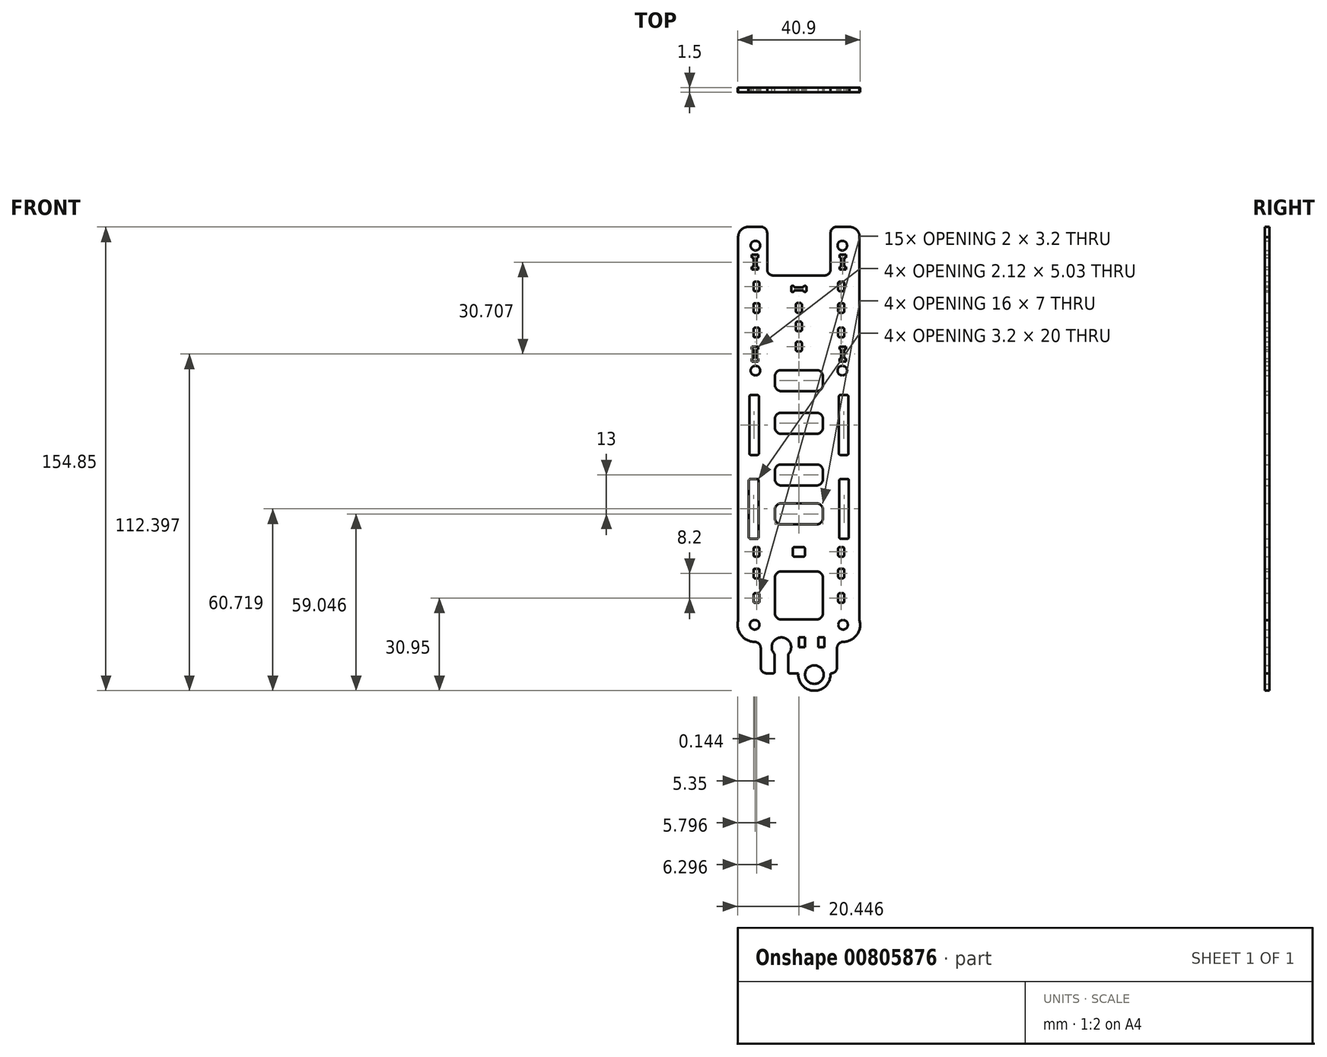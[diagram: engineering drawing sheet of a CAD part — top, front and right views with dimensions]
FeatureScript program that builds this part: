
annotation { "Feature Type Name" : "Feature", "Feature Type Description" : "" }
export const myFeature = defineFeature(function(context is Context, id is Id, definition is map)
    precondition{}
    {
        {
            var Q0;
            Q0=qCreatedBy(makeId("Front.planeOp"),FACE);
            var sketch = newSketch(context, id + "F0", { "sketchPlane" : qUnion([Q0])});
            skLineSegment(sketch, "E0", {"start": v(-16.2, 27.54) * mm, "end": v(-14.07, 27.54) * mm});
            skLineSegment(sketch, "E1", {"start": v(-14.07, 27.54) * mm, "end": v(-14.07, 26.54) * mm});
            skLineSegment(sketch, "E2", {"start": v(-14.07, 26.54) * mm, "end": v(-14.63, 26.54) * mm});
            skLineSegment(sketch, "E3", {"start": v(-14.63, 26.54) * mm, "end": v(-14.63, 23.51) * mm});
            skLineSegment(sketch, "E4", {"start": v(-14.63, 23.51) * mm, "end": v(-14.07, 23.51) * mm});
            skLineSegment(sketch, "E5", {"start": v(-14.07, 23.51) * mm, "end": v(-14.07, 22.51) * mm});
            skLineSegment(sketch, "E6", {"start": v(-14.07, 22.51) * mm, "end": v(-16.2, 22.51) * mm});
            skLineSegment(sketch, "E7", {"start": v(-16.2, 22.51) * mm, "end": v(-16.2, 23.51) * mm});
            skLineSegment(sketch, "E8", {"start": v(-16.2, 23.51) * mm, "end": v(-15.63, 23.51) * mm});
            skLineSegment(sketch, "E9", {"start": v(-15.63, 23.51) * mm, "end": v(-15.63, 26.54) * mm});
            skLineSegment(sketch, "E10", {"start": v(-15.63, 26.54) * mm, "end": v(-16.2, 26.54) * mm});
            skLineSegment(sketch, "E11", {"start": v(-16.2, 26.54) * mm, "end": v(-16.2, 27.54) * mm});
            skLineSegment(sketch, "E12", {"start": v(-20.32, 40.38) * mm, "end": v(19.03, 40.38) * mm, "construction": true});
            skLineSegment(sketch, "E13.MirrorCS", {"start": v(13.67, 23.51) * mm, "end": v(13.1, 23.51) * mm});
            skLineSegment(sketch, "E14.MirrorCS", {"start": v(15.23, 23.51) * mm, "end": v(14.67, 23.51) * mm});
            skLineSegment(sketch, "E15.MirrorCS", {"start": v(13.1, 23.51) * mm, "end": v(13.1, 22.51) * mm});
            skLineSegment(sketch, "E16.MirrorCS", {"start": v(15.23, 27.54) * mm, "end": v(13.1, 27.54) * mm});
            skLineSegment(sketch, "E17.MirrorCS", {"start": v(14.67, 26.54) * mm, "end": v(15.23, 26.54) * mm});
            skLineSegment(sketch, "E18.MirrorCS", {"start": v(15.23, 26.54) * mm, "end": v(15.23, 27.54) * mm});
            skLineSegment(sketch, "E19.MirrorCS", {"start": v(13.1, 22.51) * mm, "end": v(15.23, 22.51) * mm});
            skLineSegment(sketch, "E20.MirrorCS", {"start": v(15.23, 22.51) * mm, "end": v(15.23, 23.51) * mm});
            skLineSegment(sketch, "E21.MirrorCS", {"start": v(13.1, 27.54) * mm, "end": v(13.1, 26.54) * mm});
            skLineSegment(sketch, "E22.MirrorCS", {"start": v(13.1, 26.54) * mm, "end": v(13.67, 26.54) * mm});
            skLineSegment(sketch, "E23.MirrorCS", {"start": v(13.67, 26.54) * mm, "end": v(13.67, 23.51) * mm});
            skLineSegment(sketch, "E24.MirrorCS", {"start": v(14.67, 23.51) * mm, "end": v(14.67, 26.54) * mm});
            skLineSegment(sketch, "E25.MirrorCS", {"start": v(-14.63, 57.25) * mm, "end": v(-14.07, 57.25) * mm});
            skLineSegment(sketch, "E26.MirrorCS", {"start": v(-14.63, 54.22) * mm, "end": v(-14.63, 57.25) * mm});
            skLineSegment(sketch, "E27.MirrorCS", {"start": v(-14.07, 54.22) * mm, "end": v(-14.63, 54.22) * mm});
            skLineSegment(sketch, "E28.MirrorCS", {"start": v(-14.07, 53.22) * mm, "end": v(-14.07, 54.22) * mm});
            skLineSegment(sketch, "E29.MirrorCS", {"start": v(-16.2, 53.22) * mm, "end": v(-14.07, 53.22) * mm});
            skLineSegment(sketch, "E30.MirrorCS", {"start": v(-16.2, 54.22) * mm, "end": v(-16.2, 53.22) * mm});
            skLineSegment(sketch, "E31.MirrorCS", {"start": v(-14.07, 57.25) * mm, "end": v(-14.07, 58.25) * mm});
            skLineSegment(sketch, "E32.MirrorCS", {"start": v(-14.07, 58.25) * mm, "end": v(-16.2, 58.25) * mm});
            skLineSegment(sketch, "E33.MirrorCS", {"start": v(-15.63, 54.22) * mm, "end": v(-16.2, 54.22) * mm});
            skLineSegment(sketch, "E34.MirrorCS", {"start": v(-16.2, 58.25) * mm, "end": v(-16.2, 57.25) * mm});
            skLineSegment(sketch, "E35.MirrorCS", {"start": v(-16.2, 57.25) * mm, "end": v(-15.63, 57.25) * mm});
            skLineSegment(sketch, "E36.MirrorCS", {"start": v(-15.63, 57.25) * mm, "end": v(-15.63, 54.22) * mm});
            skLineSegment(sketch, "E37.MirrorCS", {"start": v(14.67, 54.22) * mm, "end": v(15.23, 54.22) * mm});
            skLineSegment(sketch, "E38.MirrorCS", {"start": v(14.67, 57.25) * mm, "end": v(14.67, 54.22) * mm});
            skLineSegment(sketch, "E39.MirrorCS", {"start": v(15.23, 53.22) * mm, "end": v(13.1, 53.22) * mm});
            skLineSegment(sketch, "E40.MirrorCS", {"start": v(15.23, 58.25) * mm, "end": v(15.23, 57.25) * mm});
            skLineSegment(sketch, "E41.MirrorCS", {"start": v(13.67, 54.22) * mm, "end": v(13.67, 57.25) * mm});
            skLineSegment(sketch, "E42.MirrorCS", {"start": v(13.1, 58.25) * mm, "end": v(15.23, 58.25) * mm});
            skLineSegment(sketch, "E43.MirrorCS", {"start": v(13.1, 57.25) * mm, "end": v(13.1, 58.25) * mm});
            skLineSegment(sketch, "E44.MirrorCS", {"start": v(13.1, 53.22) * mm, "end": v(13.1, 54.22) * mm});
            skLineSegment(sketch, "E45.MirrorCS", {"start": v(13.67, 57.25) * mm, "end": v(13.1, 57.25) * mm});
            skLineSegment(sketch, "E46.MirrorCS", {"start": v(15.23, 57.25) * mm, "end": v(14.67, 57.25) * mm});
            skLineSegment(sketch, "E47.MirrorCS", {"start": v(13.1, 54.22) * mm, "end": v(13.67, 54.22) * mm});
            skLineSegment(sketch, "E48.MirrorCS", {"start": v(15.23, 54.22) * mm, "end": v(15.23, 53.22) * mm});
            skCircle(sketch, "E49", {"center": v(-14.98, 61.25) * mm, "radius": 1.6 * mm});
            skCircle(sketch, "E50.MirrorC", {"center": v(14.02, 61.25) * mm, "radius": 1.6 * mm});
            skCircle(sketch, "E51", {"center": v(-15.23, -65.35) * mm, "radius": 1.6 * mm});
            skCircle(sketch, "E52.MirrorC", {"center": v(14.27, -65.35) * mm, "radius": 1.6 * mm});
            skLineSegment(sketch, "E53.bottom", {"start": v(-15.13, -39.42) * mm, "end": v(-14.13, -39.42) * mm});
            skLineSegment(sketch, "E53.top", {"start": v(-15.13, -42.62) * mm, "end": v(-14.13, -42.62) * mm});
            skLineSegment(sketch, "E53.left", {"start": v(-15.63, -39.92) * mm, "end": v(-15.63, -42.12) * mm});
            skLineSegment(sketch, "E53.right", {"start": v(-13.63, -39.92) * mm, "end": v(-13.63, -42.12) * mm});
            skLineSegment(sketch, "E54.bottom", {"start": v(-15.13, -46.62) * mm, "end": v(-14.13, -46.62) * mm});
            skLineSegment(sketch, "E54.top", {"start": v(-15.13, -49.82) * mm, "end": v(-14.13, -49.82) * mm});
            skLineSegment(sketch, "E54.left", {"start": v(-15.63, -47.12) * mm, "end": v(-15.63, -49.32) * mm});
            skLineSegment(sketch, "E54.right", {"start": v(-13.63, -47.12) * mm, "end": v(-13.63, -49.32) * mm});
            skLineSegment(sketch, "E55.bottom", {"start": v(-15.13, -54.82) * mm, "end": v(-14.13, -54.82) * mm});
            skLineSegment(sketch, "E55.top", {"start": v(-15.13, -58.02) * mm, "end": v(-14.13, -58.02) * mm});
            skLineSegment(sketch, "E55.left", {"start": v(-15.63, -55.32) * mm, "end": v(-15.63, -57.52) * mm});
            skLineSegment(sketch, "E55.right", {"start": v(-13.63, -55.32) * mm, "end": v(-13.63, -57.52) * mm});
            skPoint(sketch, "E56.visualSharp", {"position": v(-15.63, -39.42) * mm});
            skArc(sketch, "E56.filletArc", {"start": v(-15.13, -39.42) * mm, "mid": v(-15.49, -39.57) * mm, "end": v(-15.63, -39.92) * mm});
            skPoint(sketch, "E57.visualSharp", {"position": v(-13.63, -39.42) * mm});
            skArc(sketch, "E57.filletArc", {"start": v(-13.63, -39.92) * mm, "mid": v(-13.78, -39.57) * mm, "end": v(-14.13, -39.42) * mm});
            skPoint(sketch, "E58.visualSharp", {"position": v(-13.63, -42.62) * mm});
            skArc(sketch, "E58.filletArc", {"start": v(-14.13, -42.62) * mm, "mid": v(-13.78, -42.47) * mm, "end": v(-13.63, -42.12) * mm});
            skPoint(sketch, "E59.visualSharp", {"position": v(-15.63, -42.62) * mm});
            skArc(sketch, "E59.filletArc", {"start": v(-15.63, -42.12) * mm, "mid": v(-15.49, -42.47) * mm, "end": v(-15.13, -42.62) * mm});
            skPoint(sketch, "E60.visualSharp", {"position": v(-15.63, -46.62) * mm});
            skArc(sketch, "E60.filletArc", {"start": v(-15.13, -46.62) * mm, "mid": v(-15.49, -46.77) * mm, "end": v(-15.63, -47.12) * mm});
            skPoint(sketch, "E61.visualSharp", {"position": v(-13.63, -46.62) * mm});
            skArc(sketch, "E61.filletArc", {"start": v(-13.63, -47.12) * mm, "mid": v(-13.78, -46.77) * mm, "end": v(-14.13, -46.62) * mm});
            skPoint(sketch, "E62.visualSharp", {"position": v(-13.63, -49.82) * mm});
            skArc(sketch, "E62.filletArc", {"start": v(-14.13, -49.82) * mm, "mid": v(-13.78, -49.67) * mm, "end": v(-13.63, -49.32) * mm});
            skPoint(sketch, "E63.visualSharp", {"position": v(-15.63, -49.82) * mm});
            skArc(sketch, "E63.filletArc", {"start": v(-15.63, -49.32) * mm, "mid": v(-15.49, -49.67) * mm, "end": v(-15.13, -49.82) * mm});
            skPoint(sketch, "E64.visualSharp", {"position": v(-15.63, -54.82) * mm});
            skArc(sketch, "E64.filletArc", {"start": v(-15.13, -54.82) * mm, "mid": v(-15.49, -54.97) * mm, "end": v(-15.63, -55.32) * mm});
            skPoint(sketch, "E65.visualSharp", {"position": v(-13.63, -54.82) * mm});
            skArc(sketch, "E65.filletArc", {"start": v(-13.63, -55.32) * mm, "mid": v(-13.78, -54.97) * mm, "end": v(-14.13, -54.82) * mm});
            skPoint(sketch, "E66.visualSharp", {"position": v(-13.63, -58.02) * mm});
            skArc(sketch, "E66.filletArc", {"start": v(-14.13, -58.02) * mm, "mid": v(-13.78, -57.87) * mm, "end": v(-13.63, -57.52) * mm});
            skPoint(sketch, "E67.visualSharp", {"position": v(-15.63, -58.02) * mm});
            skArc(sketch, "E67.filletArc", {"start": v(-15.63, -57.52) * mm, "mid": v(-15.49, -57.87) * mm, "end": v(-15.13, -58.02) * mm});
            skArc(sketch, "E68.MirrorCS", {"start": v(14.17, -54.82) * mm, "mid": v(14.52, -54.97) * mm, "end": v(14.67, -55.32) * mm});
            skArc(sketch, "E69.MirrorCS", {"start": v(13.17, -58.02) * mm, "mid": v(12.81, -57.87) * mm, "end": v(12.67, -57.52) * mm});
            skArc(sketch, "E70.MirrorCS", {"start": v(12.67, -39.92) * mm, "mid": v(12.81, -39.57) * mm, "end": v(13.17, -39.42) * mm});
            skArc(sketch, "E71.MirrorCS", {"start": v(14.17, -39.42) * mm, "mid": v(14.52, -39.57) * mm, "end": v(14.67, -39.92) * mm});
            skArc(sketch, "E72.MirrorCS", {"start": v(14.67, -49.32) * mm, "mid": v(14.52, -49.67) * mm, "end": v(14.17, -49.82) * mm});
            skArc(sketch, "E73.MirrorCS", {"start": v(12.67, -55.32) * mm, "mid": v(12.81, -54.97) * mm, "end": v(13.17, -54.82) * mm});
            skArc(sketch, "E74.MirrorCS", {"start": v(14.67, -57.52) * mm, "mid": v(14.52, -57.87) * mm, "end": v(14.17, -58.02) * mm});
            skArc(sketch, "E75.MirrorCS", {"start": v(13.17, -42.62) * mm, "mid": v(12.81, -42.47) * mm, "end": v(12.67, -42.12) * mm});
            skArc(sketch, "E76.MirrorCS", {"start": v(13.17, -49.82) * mm, "mid": v(12.81, -49.67) * mm, "end": v(12.67, -49.32) * mm});
            skArc(sketch, "E77.MirrorCS", {"start": v(12.67, -47.12) * mm, "mid": v(12.81, -46.77) * mm, "end": v(13.17, -46.62) * mm});
            skArc(sketch, "E78.MirrorCS", {"start": v(14.17, -46.62) * mm, "mid": v(14.52, -46.77) * mm, "end": v(14.67, -47.12) * mm});
            skArc(sketch, "E79.MirrorCS", {"start": v(14.67, -42.12) * mm, "mid": v(14.52, -42.47) * mm, "end": v(14.17, -42.62) * mm});
            skPoint(sketch, "E80.MirrorP", {"position": v(12.67, -46.62) * mm});
            skLineSegment(sketch, "E81.MirrorCS", {"start": v(14.17, -46.62) * mm, "end": v(13.17, -46.62) * mm});
            skLineSegment(sketch, "E82.MirrorCS", {"start": v(14.67, -47.12) * mm, "end": v(14.67, -49.32) * mm});
            skPoint(sketch, "E83.MirrorP", {"position": v(14.67, -54.82) * mm});
            skPoint(sketch, "E84.MirrorP", {"position": v(14.67, -39.42) * mm});
            skLineSegment(sketch, "E85.MirrorCS", {"start": v(12.67, -39.92) * mm, "end": v(12.67, -42.12) * mm});
            skPoint(sketch, "E86.MirrorP", {"position": v(12.67, -58.02) * mm});
            skLineSegment(sketch, "E87.MirrorCS", {"start": v(14.17, -49.82) * mm, "end": v(13.17, -49.82) * mm});
            skPoint(sketch, "E88.MirrorP", {"position": v(12.67, -42.62) * mm});
            skLineSegment(sketch, "E89.MirrorCS", {"start": v(14.17, -39.42) * mm, "end": v(13.17, -39.42) * mm});
            skPoint(sketch, "E90.MirrorP", {"position": v(14.67, -42.62) * mm});
            skPoint(sketch, "E91.MirrorP", {"position": v(14.67, -58.02) * mm});
            skLineSegment(sketch, "E92.MirrorCS", {"start": v(12.67, -47.12) * mm, "end": v(12.67, -49.32) * mm});
            skPoint(sketch, "E93.MirrorP", {"position": v(12.67, -39.42) * mm});
            skPoint(sketch, "E94.MirrorP", {"position": v(12.67, -54.82) * mm});
            skLineSegment(sketch, "E95.MirrorCS", {"start": v(12.67, -55.32) * mm, "end": v(12.67, -57.52) * mm});
            skPoint(sketch, "E96.MirrorP", {"position": v(14.67, -46.62) * mm});
            skLineSegment(sketch, "E97.MirrorCS", {"start": v(14.67, -39.92) * mm, "end": v(14.67, -42.12) * mm});
            skLineSegment(sketch, "E98.MirrorCS", {"start": v(14.17, -58.02) * mm, "end": v(13.17, -58.02) * mm});
            skLineSegment(sketch, "E99.MirrorCS", {"start": v(14.67, -55.32) * mm, "end": v(14.67, -57.52) * mm});
            skPoint(sketch, "E100.MirrorP", {"position": v(14.67, -49.82) * mm});
            skLineSegment(sketch, "E101.MirrorCS", {"start": v(14.17, -42.62) * mm, "end": v(13.17, -42.62) * mm});
            skPoint(sketch, "E102.MirrorP", {"position": v(12.67, -49.82) * mm});
            skLineSegment(sketch, "E103.MirrorCS", {"start": v(14.17, -54.82) * mm, "end": v(13.17, -54.82) * mm});
            skLineSegment(sketch, "E104", {"start": v(-20.73, 64.37) * mm, "end": v(-20.73, -63.85) * mm});
            skLineSegment(sketch, "E105.MirrorCS", {"start": v(19.77, 64.37) * mm, "end": v(19.77, -63.85) * mm});
            skArc(sketch, "E106", {"start": v(-17.39, 67.48) * mm, "mid": v(-19.81, 66.5) * mm, "end": v(-20.73, 64.04) * mm});
            skArc(sketch, "E107.MirrorCS", {"start": v(16.42, 67.48) * mm, "mid": v(18.84, 66.5) * mm, "end": v(19.77, 64.04) * mm});
            skPoint(sketch, "E108.orphan", {"position": v(-20.73, 67.03) * mm});
            skPoint(sketch, "E109.orphan", {"position": v(19.77, 67.03) * mm});
            skLineSegment(sketch, "E110", {"start": v(-17.39, 67.48) * mm, "end": v(-13.07, 67.48) * mm});
            skLineSegment(sketch, "E111", {"start": v(-11.07, 65.48) * mm, "end": v(-11.07, 53.27) * mm});
            skLineSegment(sketch, "E112", {"start": v(-9.07, 51.27) * mm, "end": v(-0.48, 51.27) * mm});
            skLineSegment(sketch, "E113.MirrorCS", {"start": v(16.42, 67.48) * mm, "end": v(12.1, 67.48) * mm});
            skLineSegment(sketch, "E114.MirrorCS", {"start": v(10.1, 65.48) * mm, "end": v(10.1, 53.27) * mm});
            skLineSegment(sketch, "E115.MirrorCS", {"start": v(8.1, 51.27) * mm, "end": v(-0.48, 51.27) * mm});
            skPoint(sketch, "E116.orphan", {"position": v(-14.5, 62.78) * mm});
            skPoint(sketch, "E117.orphan", {"position": v(13.54, 62.78) * mm});
            skPoint(sketch, "E118.visualSharp", {"position": v(-11.07, 67.48) * mm});
            skArc(sketch, "E118.filletArc", {"start": v(-11.07, 65.48) * mm, "mid": v(-11.65, 66.9) * mm, "end": v(-13.07, 67.48) * mm});
            skPoint(sketch, "E119.visualSharp", {"position": v(10.1, 67.48) * mm});
            skArc(sketch, "E119.filletArc", {"start": v(12.1, 67.48) * mm, "mid": v(10.69, 66.9) * mm, "end": v(10.1, 65.48) * mm});
            skPoint(sketch, "E120.visualSharp", {"position": v(10.1, 51.27) * mm});
            skArc(sketch, "E120.filletArc", {"start": v(8.1, 51.27) * mm, "mid": v(9.51, 51.85) * mm, "end": v(10.1, 53.27) * mm});
            skPoint(sketch, "E121.visualSharp", {"position": v(-11.07, 51.27) * mm});
            skArc(sketch, "E121.filletArc", {"start": v(-11.07, 53.27) * mm, "mid": v(-10.48, 51.85) * mm, "end": v(-9.07, 51.27) * mm});
            skCircle(sketch, "E122", {"center": v(-14.98, 19.5) * mm, "radius": 1.6 * mm});
            skCircle(sketch, "E123.MirrorC", {"center": v(14.02, 19.5) * mm, "radius": 1.6 * mm});
            skLineSegment(sketch, "E124", {"start": v(-13.24, -73.05) * mm, "end": v(-13.24, -79.57) * mm});
            skLineSegment(sketch, "E125", {"start": v(-11.24, -81.57) * mm, "end": v(-9.08, -81.57) * mm});
            skLineSegment(sketch, "E126.MirrorCS", {"start": v(12.27, -73.05) * mm, "end": v(12.27, -79.57) * mm});
            skLineSegment(sketch, "E127.MirrorCS", {"start": v(10.27, -81.57) * mm, "end": v(10.05, -81.57) * mm});
            skArc(sketch, "E128", {"start": v(-0.66, -81.57) * mm, "mid": v(4.7, -87.37) * mm, "end": v(10.05, -81.57) * mm});
            skPoint(sketch, "E129.end.orphan", {"position": v(-0.48, -65.48) * mm});
            skPoint(sketch, "E130.orphan", {"position": v(8.67, -69.6) * mm});
            skPoint(sketch, "E131.orphan", {"position": v(-9.64, -69.6) * mm});
            skPoint(sketch, "E132.visualSharp", {"position": v(12.27, -81.57) * mm});
            skArc(sketch, "E132.filletArc", {"start": v(10.27, -81.57) * mm, "mid": v(11.68, -80.99) * mm, "end": v(12.27, -79.57) * mm});
            skPoint(sketch, "E133.visualSharp", {"position": v(-13.24, -81.57) * mm});
            skArc(sketch, "E133.filletArc", {"start": v(-13.24, -79.57) * mm, "mid": v(-12.65, -80.99) * mm, "end": v(-11.24, -81.57) * mm});
            skPoint(sketch, "E134.visualSharp", {"position": v(-13.24, -70.76) * mm});
            skArc(sketch, "E134.filletArc", {"start": v(-13.24, -73.05) * mm, "mid": v(-13.82, -71.64) * mm, "end": v(-15.24, -71.05) * mm});
            skPoint(sketch, "E135.visualSharp", {"position": v(12.27, -70.76) * mm});
            skArc(sketch, "E135.filletArc", {"start": v(14.27, -71.05) * mm, "mid": v(12.85, -71.64) * mm, "end": v(12.27, -73.05) * mm});
            skCircle(sketch, "E136", {"center": v(4.7, -82) * mm, "radius": 3.1 * mm});
            skArc(sketch, "E137", {"start": v(-20.73, -63.85) * mm, "mid": v(-19.76, -68.81) * mm, "end": v(-15.24, -71.05) * mm});
            skArc(sketch, "E138.MirrorC", {"start": v(19.77, -63.85) * mm, "mid": v(18.8, -68.81) * mm, "end": v(14.27, -71.05) * mm});
            skPoint(sketch, "E139.orphan", {"position": v(-0.48, -81.57) * mm});
            skLineSegment(sketch, "E140", {"start": v(-3.05, 46.24) * mm, "end": v(-3.05, 47.36) * mm});
            skLineSegment(sketch, "E141", {"start": v(-2.55, 47.86) * mm, "end": v(-2.55, 47.86) * mm});
            skLineSegment(sketch, "E142", {"start": v(-2.05, 47.36) * mm, "end": v(-2.05, 47.3) * mm});
            skLineSegment(sketch, "E143", {"start": v(-2.05, 47.3) * mm, "end": v(-0.48, 47.3) * mm});
            skLineSegment(sketch, "E144", {"start": v(-2.55, 45.74) * mm, "end": v(-2.55, 45.74) * mm});
            skLineSegment(sketch, "E145", {"start": v(-2.05, 46.24) * mm, "end": v(-2.05, 46.3) * mm});
            skLineSegment(sketch, "E146", {"start": v(-2.05, 46.3) * mm, "end": v(-0.48, 46.3) * mm});
            skLineSegment(sketch, "E147.MirrorCS", {"start": v(1.03, 46.3) * mm, "end": v(-0.48, 46.3) * mm});
            skLineSegment(sketch, "E148.MirrorCS", {"start": v(1.53, 45.74) * mm, "end": v(1.53, 45.74) * mm});
            skLineSegment(sketch, "E149.MirrorCS", {"start": v(1.03, 46.24) * mm, "end": v(1.03, 46.3) * mm});
            skLineSegment(sketch, "E150.MirrorCS", {"start": v(1.03, 47.3) * mm, "end": v(-0.48, 47.3) * mm});
            skLineSegment(sketch, "E151.MirrorCS", {"start": v(2.03, 46.24) * mm, "end": v(2.03, 47.36) * mm});
            skLineSegment(sketch, "E152.MirrorCS", {"start": v(1.53, 47.86) * mm, "end": v(1.53, 47.86) * mm});
            skLineSegment(sketch, "E153.MirrorCS", {"start": v(1.03, 47.36) * mm, "end": v(1.03, 47.3) * mm});
            skPoint(sketch, "E154.visualSharp", {"position": v(-3.05, 47.86) * mm});
            skArc(sketch, "E154.filletArc", {"start": v(-2.55, 47.86) * mm, "mid": v(-2.9, 47.71) * mm, "end": v(-3.05, 47.36) * mm});
            skPoint(sketch, "E155.visualSharp", {"position": v(-2.05, 47.86) * mm});
            skArc(sketch, "E155.filletArc", {"start": v(-2.05, 47.36) * mm, "mid": v(-2.2, 47.71) * mm, "end": v(-2.55, 47.86) * mm});
            skPoint(sketch, "E156.visualSharp", {"position": v(-2.05, 45.74) * mm});
            skArc(sketch, "E156.filletArc", {"start": v(-2.55, 45.74) * mm, "mid": v(-2.2, 45.89) * mm, "end": v(-2.05, 46.24) * mm});
            skPoint(sketch, "E157.visualSharp", {"position": v(-3.05, 45.74) * mm});
            skArc(sketch, "E157.filletArc", {"start": v(-3.05, 46.24) * mm, "mid": v(-2.9, 45.89) * mm, "end": v(-2.55, 45.74) * mm});
            skPoint(sketch, "E158.visualSharp", {"position": v(2.03, 47.86) * mm});
            skArc(sketch, "E158.filletArc", {"start": v(2.03, 47.36) * mm, "mid": v(1.89, 47.71) * mm, "end": v(1.53, 47.86) * mm});
            skPoint(sketch, "E159.visualSharp", {"position": v(1.03, 47.86) * mm});
            skArc(sketch, "E159.filletArc", {"start": v(1.53, 47.86) * mm, "mid": v(1.18, 47.71) * mm, "end": v(1.03, 47.36) * mm});
            skPoint(sketch, "E160.visualSharp", {"position": v(2.03, 45.74) * mm});
            skArc(sketch, "E160.filletArc", {"start": v(1.53, 45.74) * mm, "mid": v(1.89, 45.89) * mm, "end": v(2.03, 46.24) * mm});
            skPoint(sketch, "E161.visualSharp", {"position": v(1.03, 45.74) * mm});
            skArc(sketch, "E161.filletArc", {"start": v(1.03, 46.24) * mm, "mid": v(1.18, 45.89) * mm, "end": v(1.53, 45.74) * mm});
            skLineSegment(sketch, "E162.bottom", {"start": v(-16.54, 11.35) * mm, "end": v(-14.34, 11.35) * mm});
            skLineSegment(sketch, "E162.top", {"start": v(-16.54, -8.65) * mm, "end": v(-14.34, -8.65) * mm});
            skLineSegment(sketch, "E162.left", {"start": v(-17.04, 10.85) * mm, "end": v(-17.04, -8.15) * mm});
            skLineSegment(sketch, "E162.right", {"start": v(-13.84, 10.85) * mm, "end": v(-13.84, -8.15) * mm});
            skLineSegment(sketch, "E163.bottom", {"start": v(-16.68, -16.65) * mm, "end": v(-14.48, -16.65) * mm});
            skLineSegment(sketch, "E163.top", {"start": v(-16.68, -36.65) * mm, "end": v(-14.48, -36.65) * mm});
            skLineSegment(sketch, "E163.left", {"start": v(-17.18, -17.15) * mm, "end": v(-17.18, -36.15) * mm});
            skLineSegment(sketch, "E163.right", {"start": v(-13.98, -17.15) * mm, "end": v(-13.98, -36.15) * mm});
            skLineSegment(sketch, "E164.bottom", {"start": v(-6.48, 19.68) * mm, "end": v(5.52, 19.68) * mm});
            skLineSegment(sketch, "E164.top", {"start": v(-6.48, 12.68) * mm, "end": v(5.52, 12.68) * mm});
            skLineSegment(sketch, "E164.left", {"start": v(-8.48, 17.68) * mm, "end": v(-8.48, 14.68) * mm});
            skLineSegment(sketch, "E164.right", {"start": v(7.52, 17.68) * mm, "end": v(7.52, 14.68) * mm});
            skLineSegment(sketch, "E165.bottom", {"start": v(-6.48, -24.82) * mm, "end": v(5.52, -24.82) * mm});
            skLineSegment(sketch, "E165.top", {"start": v(-6.48, -31.82) * mm, "end": v(5.52, -31.82) * mm});
            skLineSegment(sketch, "E165.left", {"start": v(-8.48, -26.82) * mm, "end": v(-8.48, -29.82) * mm});
            skLineSegment(sketch, "E165.right", {"start": v(7.52, -26.82) * mm, "end": v(7.52, -29.82) * mm});
            skLineSegment(sketch, "E166.bottom", {"start": v(-6.48, -47.57) * mm, "end": v(5.52, -47.57) * mm});
            skLineSegment(sketch, "E166.top", {"start": v(-6.48, -63.57) * mm, "end": v(5.52, -63.57) * mm});
            skLineSegment(sketch, "E166.left", {"start": v(-8.48, -49.57) * mm, "end": v(-8.48, -61.57) * mm});
            skLineSegment(sketch, "E166.right", {"start": v(7.52, -49.57) * mm, "end": v(7.52, -61.57) * mm});
            skLineSegment(sketch, "E167.bottom", {"start": v(-6.48, 5.43) * mm, "end": v(5.52, 5.43) * mm});
            skLineSegment(sketch, "E167.top", {"start": v(-6.48, -1.57) * mm, "end": v(5.52, -1.57) * mm});
            skLineSegment(sketch, "E167.left", {"start": v(-8.48, 3.43) * mm, "end": v(-8.48, 0.43) * mm});
            skLineSegment(sketch, "E167.right", {"start": v(7.52, 3.43) * mm, "end": v(7.52, 0.43) * mm});
            skLineSegment(sketch, "E168.bottom", {"start": v(-6.48, -11.82) * mm, "end": v(5.52, -11.82) * mm});
            skLineSegment(sketch, "E168.top", {"start": v(-6.48, -18.82) * mm, "end": v(5.52, -18.82) * mm});
            skLineSegment(sketch, "E168.left", {"start": v(-8.48, -13.82) * mm, "end": v(-8.48, -16.82) * mm});
            skLineSegment(sketch, "E168.right", {"start": v(7.52, -13.82) * mm, "end": v(7.52, -16.82) * mm});
            skPoint(sketch, "E169.visualSharp", {"position": v(-8.48, -47.57) * mm});
            skArc(sketch, "E169.filletArc", {"start": v(-6.48, -47.57) * mm, "mid": v(-7.9, -48.16) * mm, "end": v(-8.48, -49.57) * mm});
            skPoint(sketch, "E170.visualSharp", {"position": v(7.52, -47.57) * mm});
            skArc(sketch, "E170.filletArc", {"start": v(7.52, -49.57) * mm, "mid": v(6.93, -48.16) * mm, "end": v(5.52, -47.57) * mm});
            skPoint(sketch, "E171.visualSharp", {"position": v(7.52, -63.57) * mm});
            skArc(sketch, "E171.filletArc", {"start": v(5.52, -63.57) * mm, "mid": v(6.93, -62.99) * mm, "end": v(7.52, -61.57) * mm});
            skPoint(sketch, "E172.visualSharp", {"position": v(-8.48, -63.57) * mm});
            skArc(sketch, "E172.filletArc", {"start": v(-8.48, -61.57) * mm, "mid": v(-7.9, -62.99) * mm, "end": v(-6.48, -63.57) * mm});
            skLineSegment(sketch, "E173.bottom", {"start": v(-1.98, -39.42) * mm, "end": v(1.02, -39.42) * mm});
            skLineSegment(sketch, "E173.top", {"start": v(-1.98, -42.62) * mm, "end": v(1.02, -42.62) * mm});
            skLineSegment(sketch, "E173.left", {"start": v(-2.48, -39.92) * mm, "end": v(-2.48, -42.12) * mm});
            skLineSegment(sketch, "E173.right", {"start": v(1.52, -39.92) * mm, "end": v(1.52, -42.12) * mm});
            skPoint(sketch, "E174.visualSharp", {"position": v(-2.48, -39.42) * mm});
            skArc(sketch, "E174.filletArc", {"start": v(-1.98, -39.42) * mm, "mid": v(-2.34, -39.57) * mm, "end": v(-2.48, -39.92) * mm});
            skPoint(sketch, "E175.visualSharp", {"position": v(1.52, -39.42) * mm});
            skArc(sketch, "E175.filletArc", {"start": v(1.52, -39.92) * mm, "mid": v(1.37, -39.57) * mm, "end": v(1.02, -39.42) * mm});
            skPoint(sketch, "E176.visualSharp", {"position": v(1.52, -42.62) * mm});
            skArc(sketch, "E176.filletArc", {"start": v(1.02, -42.62) * mm, "mid": v(1.37, -42.47) * mm, "end": v(1.52, -42.12) * mm});
            skPoint(sketch, "E177.visualSharp", {"position": v(-2.48, -42.62) * mm});
            skArc(sketch, "E177.filletArc", {"start": v(-2.48, -42.12) * mm, "mid": v(-2.34, -42.47) * mm, "end": v(-1.98, -42.62) * mm});
            skPoint(sketch, "E178.visualSharp", {"position": v(-8.48, -31.82) * mm});
            skArc(sketch, "E178.filletArc", {"start": v(-8.48, -29.82) * mm, "mid": v(-7.9, -31.24) * mm, "end": v(-6.48, -31.82) * mm});
            skPoint(sketch, "E179.visualSharp", {"position": v(7.52, -31.82) * mm});
            skArc(sketch, "E179.filletArc", {"start": v(5.52, -31.82) * mm, "mid": v(6.93, -31.24) * mm, "end": v(7.52, -29.82) * mm});
            skPoint(sketch, "E180.visualSharp", {"position": v(7.52, -24.82) * mm});
            skArc(sketch, "E180.filletArc", {"start": v(7.52, -26.82) * mm, "mid": v(6.93, -25.41) * mm, "end": v(5.52, -24.82) * mm});
            skPoint(sketch, "E181.visualSharp", {"position": v(-8.48, -24.82) * mm});
            skArc(sketch, "E181.filletArc", {"start": v(-6.48, -24.82) * mm, "mid": v(-7.9, -25.41) * mm, "end": v(-8.48, -26.82) * mm});
            skPoint(sketch, "E182.visualSharp", {"position": v(-8.48, -11.82) * mm});
            skArc(sketch, "E182.filletArc", {"start": v(-6.48, -11.82) * mm, "mid": v(-7.9, -12.41) * mm, "end": v(-8.48, -13.82) * mm});
            skPoint(sketch, "E183.visualSharp", {"position": v(-8.48, -18.82) * mm});
            skArc(sketch, "E183.filletArc", {"start": v(-8.48, -16.82) * mm, "mid": v(-7.9, -18.24) * mm, "end": v(-6.48, -18.82) * mm});
            skPoint(sketch, "E184.visualSharp", {"position": v(7.52, -18.82) * mm});
            skArc(sketch, "E184.filletArc", {"start": v(5.52, -18.82) * mm, "mid": v(6.93, -18.24) * mm, "end": v(7.52, -16.82) * mm});
            skPoint(sketch, "E185.visualSharp", {"position": v(7.52, -11.82) * mm});
            skArc(sketch, "E185.filletArc", {"start": v(7.52, -13.82) * mm, "mid": v(6.93, -12.41) * mm, "end": v(5.52, -11.82) * mm});
            skPoint(sketch, "E186.visualSharp", {"position": v(7.52, -1.57) * mm});
            skArc(sketch, "E186.filletArc", {"start": v(5.52, -1.57) * mm, "mid": v(6.93, -0.99) * mm, "end": v(7.52, 0.43) * mm});
            skPoint(sketch, "E187.visualSharp", {"position": v(7.52, 5.43) * mm});
            skArc(sketch, "E187.filletArc", {"start": v(7.52, 3.43) * mm, "mid": v(6.93, 4.84) * mm, "end": v(5.52, 5.43) * mm});
            skPoint(sketch, "E188.visualSharp", {"position": v(-8.48, 5.43) * mm});
            skArc(sketch, "E188.filletArc", {"start": v(-6.48, 5.43) * mm, "mid": v(-7.9, 4.84) * mm, "end": v(-8.48, 3.43) * mm});
            skPoint(sketch, "E189.visualSharp", {"position": v(-8.48, -1.57) * mm});
            skArc(sketch, "E189.filletArc", {"start": v(-8.48, 0.43) * mm, "mid": v(-7.9, -0.99) * mm, "end": v(-6.48, -1.57) * mm});
            skPoint(sketch, "E190.visualSharp", {"position": v(-8.48, 19.68) * mm});
            skArc(sketch, "E190.filletArc", {"start": v(-6.48, 19.68) * mm, "mid": v(-7.9, 19.09) * mm, "end": v(-8.48, 17.68) * mm});
            skPoint(sketch, "E191.visualSharp", {"position": v(7.52, 19.68) * mm});
            skArc(sketch, "E191.filletArc", {"start": v(7.52, 17.68) * mm, "mid": v(6.93, 19.09) * mm, "end": v(5.52, 19.68) * mm});
            skPoint(sketch, "E192.visualSharp", {"position": v(7.52, 12.68) * mm});
            skArc(sketch, "E192.filletArc", {"start": v(5.52, 12.68) * mm, "mid": v(6.93, 13.26) * mm, "end": v(7.52, 14.68) * mm});
            skPoint(sketch, "E193.visualSharp", {"position": v(-8.48, 12.68) * mm});
            skArc(sketch, "E193.filletArc", {"start": v(-8.48, 14.68) * mm, "mid": v(-7.9, 13.26) * mm, "end": v(-6.48, 12.68) * mm});
            skPoint(sketch, "E194.visualSharp", {"position": v(-17.04, 11.35) * mm});
            skArc(sketch, "E194.filletArc", {"start": v(-16.54, 11.35) * mm, "mid": v(-16.89, 11.2) * mm, "end": v(-17.04, 10.85) * mm});
            skPoint(sketch, "E195.visualSharp", {"position": v(-13.84, 11.35) * mm});
            skArc(sketch, "E195.filletArc", {"start": v(-13.84, 10.85) * mm, "mid": v(-13.98, 11.2) * mm, "end": v(-14.34, 11.35) * mm});
            skPoint(sketch, "E196.visualSharp", {"position": v(-13.84, -8.65) * mm});
            skArc(sketch, "E196.filletArc", {"start": v(-14.34, -8.65) * mm, "mid": v(-13.98, -8.5) * mm, "end": v(-13.84, -8.15) * mm});
            skPoint(sketch, "E197.visualSharp", {"position": v(-17.04, -8.65) * mm});
            skArc(sketch, "E197.filletArc", {"start": v(-17.04, -8.15) * mm, "mid": v(-16.89, -8.5) * mm, "end": v(-16.54, -8.65) * mm});
            skPoint(sketch, "E198.visualSharp", {"position": v(-17.18, -16.65) * mm});
            skArc(sketch, "E198.filletArc", {"start": v(-16.68, -16.65) * mm, "mid": v(-17.03, -16.8) * mm, "end": v(-17.18, -17.15) * mm});
            skPoint(sketch, "E199.visualSharp", {"position": v(-13.98, -16.65) * mm});
            skArc(sketch, "E199.filletArc", {"start": v(-13.98, -17.15) * mm, "mid": v(-14.13, -16.8) * mm, "end": v(-14.48, -16.65) * mm});
            skPoint(sketch, "E200.visualSharp", {"position": v(-13.98, -36.65) * mm});
            skArc(sketch, "E200.filletArc", {"start": v(-14.48, -36.65) * mm, "mid": v(-14.13, -36.5) * mm, "end": v(-13.98, -36.15) * mm});
            skPoint(sketch, "E201.visualSharp", {"position": v(-17.18, -36.65) * mm});
            skArc(sketch, "E201.filletArc", {"start": v(-17.18, -36.15) * mm, "mid": v(-17.03, -36.5) * mm, "end": v(-16.68, -36.65) * mm});
            skArc(sketch, "E202", {"start": v(-4.02, -75.15) * mm, "mid": v(-6.3, -69.58) * mm, "end": v(-8.58, -75.15) * mm});
            skLineSegment(sketch, "E203", {"start": v(-8.58, -75.15) * mm, "end": v(-8.58, -81.07) * mm});
            skLineSegment(sketch, "E204", {"start": v(-6.3, -72.83) * mm, "end": v(-6.3, -81.57) * mm, "construction": true});
            skLineSegment(sketch, "E205.MirrorCS", {"start": v(-4.02, -75.15) * mm, "end": v(-4.02, -81.07) * mm});
            skLineSegment(sketch, "E206.trimOffspring", {"start": v(-3.52, -81.57) * mm, "end": v(-0.66, -81.57) * mm});
            skPoint(sketch, "E207.visualSharp", {"position": v(-4.02, -81.57) * mm});
            skArc(sketch, "E207.filletArc", {"start": v(-4.02, -81.07) * mm, "mid": v(-3.87, -81.43) * mm, "end": v(-3.52, -81.57) * mm});
            skPoint(sketch, "E208.visualSharp", {"position": v(-8.58, -81.57) * mm});
            skArc(sketch, "E208.filletArc", {"start": v(-9.08, -81.57) * mm, "mid": v(-8.73, -81.43) * mm, "end": v(-8.58, -81.07) * mm});
            skLineSegment(sketch, "E209.bottom", {"start": v(-0.48, -69.57) * mm, "end": v(1.52, -69.57) * mm});
            skLineSegment(sketch, "E209.top", {"start": v(-0.48, -72.77) * mm, "end": v(1.52, -72.77) * mm});
            skLineSegment(sketch, "E209.left", {"start": v(-0.48, -69.57) * mm, "end": v(-0.48, -72.77) * mm});
            skLineSegment(sketch, "E209.right", {"start": v(1.52, -69.57) * mm, "end": v(1.52, -72.77) * mm});
            skLineSegment(sketch, "E210.bottom", {"start": v(6.02, -69.57) * mm, "end": v(8.02, -69.57) * mm});
            skLineSegment(sketch, "E210.top", {"start": v(6.02, -72.77) * mm, "end": v(8.02, -72.77) * mm});
            skLineSegment(sketch, "E210.left", {"start": v(6.02, -69.57) * mm, "end": v(6.02, -72.77) * mm});
            skLineSegment(sketch, "E210.right", {"start": v(8.02, -69.57) * mm, "end": v(8.02, -72.77) * mm});
            skArc(sketch, "E211.MirrorCS", {"start": v(15.71, -16.65) * mm, "mid": v(16.07, -16.8) * mm, "end": v(16.21, -17.15) * mm});
            skArc(sketch, "E212.MirrorCS", {"start": v(16.21, -36.15) * mm, "mid": v(16.07, -36.5) * mm, "end": v(15.71, -36.65) * mm});
            skArc(sketch, "E213.MirrorCS", {"start": v(13.01, -17.15) * mm, "mid": v(13.16, -16.8) * mm, "end": v(13.51, -16.65) * mm});
            skArc(sketch, "E214.MirrorCS", {"start": v(13.51, -36.65) * mm, "mid": v(13.16, -36.5) * mm, "end": v(13.01, -36.15) * mm});
            skLineSegment(sketch, "E215.MirrorCS", {"start": v(15.71, -16.65) * mm, "end": v(13.51, -16.65) * mm});
            skLineSegment(sketch, "E216.MirrorCS", {"start": v(15.71, -36.65) * mm, "end": v(13.51, -36.65) * mm});
            skPoint(sketch, "E217.MirrorP", {"position": v(16.21, -36.65) * mm});
            skPoint(sketch, "E218.MirrorP", {"position": v(13.01, -36.65) * mm});
            skPoint(sketch, "E219.MirrorP", {"position": v(16.21, -16.65) * mm});
            skLineSegment(sketch, "E220.MirrorCS", {"start": v(16.21, -17.15) * mm, "end": v(16.21, -36.15) * mm});
            skLineSegment(sketch, "E221.MirrorCS", {"start": v(13.01, -17.15) * mm, "end": v(13.01, -36.15) * mm});
            skPoint(sketch, "E222.MirrorP", {"position": v(13.01, -16.65) * mm});
            skArc(sketch, "E223.MirrorCS", {"start": v(16.07, -8.15) * mm, "mid": v(15.92, -8.5) * mm, "end": v(15.57, -8.65) * mm});
            skArc(sketch, "E224.MirrorCS", {"start": v(13.37, -8.65) * mm, "mid": v(13.01, -8.5) * mm, "end": v(12.87, -8.15) * mm});
            skArc(sketch, "E225.MirrorCS", {"start": v(15.57, 11.35) * mm, "mid": v(15.92, 11.2) * mm, "end": v(16.07, 10.85) * mm});
            skArc(sketch, "E226.MirrorCS", {"start": v(12.87, 10.85) * mm, "mid": v(13.01, 11.2) * mm, "end": v(13.37, 11.35) * mm});
            skLineSegment(sketch, "E227.MirrorCS", {"start": v(15.57, -8.65) * mm, "end": v(13.37, -8.65) * mm});
            skLineSegment(sketch, "E228.MirrorCS", {"start": v(15.57, 11.35) * mm, "end": v(13.37, 11.35) * mm});
            skLineSegment(sketch, "E229.MirrorCS", {"start": v(16.07, 10.85) * mm, "end": v(16.07, -8.15) * mm});
            skLineSegment(sketch, "E230.MirrorCS", {"start": v(12.87, 10.85) * mm, "end": v(12.87, -8.15) * mm});
            skPoint(sketch, "E231.MirrorP", {"position": v(12.87, -8.65) * mm});
            skPoint(sketch, "E232.MirrorP", {"position": v(16.07, -8.65) * mm});
            skPoint(sketch, "E233.MirrorP", {"position": v(12.87, 11.35) * mm});
            skPoint(sketch, "E234.MirrorP", {"position": v(16.07, 11.35) * mm});
            skLineSegment(sketch, "E235.bottom", {"start": v(-15.13, 49.22) * mm, "end": v(-14.13, 49.22) * mm});
            skLineSegment(sketch, "E235.top", {"start": v(-15.13, 46.02) * mm, "end": v(-14.13, 46.02) * mm});
            skLineSegment(sketch, "E235.left", {"start": v(-15.63, 48.72) * mm, "end": v(-15.63, 46.52) * mm});
            skLineSegment(sketch, "E235.right", {"start": v(-13.63, 48.72) * mm, "end": v(-13.63, 46.52) * mm});
            skLineSegment(sketch, "E236.bottom", {"start": v(-15.13, 42.02) * mm, "end": v(-14.13, 42.02) * mm});
            skLineSegment(sketch, "E236.top", {"start": v(-15.13, 38.82) * mm, "end": v(-14.13, 38.82) * mm});
            skLineSegment(sketch, "E236.left", {"start": v(-15.63, 41.52) * mm, "end": v(-15.63, 39.32) * mm});
            skLineSegment(sketch, "E236.right", {"start": v(-13.63, 41.52) * mm, "end": v(-13.63, 39.32) * mm});
            skLineSegment(sketch, "E237.bottom", {"start": v(-15.13, 33.82) * mm, "end": v(-14.13, 33.82) * mm});
            skLineSegment(sketch, "E237.top", {"start": v(-15.13, 30.62) * mm, "end": v(-14.13, 30.62) * mm});
            skLineSegment(sketch, "E237.left", {"start": v(-15.63, 33.32) * mm, "end": v(-15.63, 31.12) * mm});
            skLineSegment(sketch, "E237.right", {"start": v(-13.63, 33.32) * mm, "end": v(-13.63, 31.12) * mm});
            skPoint(sketch, "E238.visualSharp", {"position": v(-15.63, 49.22) * mm});
            skArc(sketch, "E238.filletArc", {"start": v(-15.13, 49.22) * mm, "mid": v(-15.49, 49.07) * mm, "end": v(-15.63, 48.72) * mm});
            skPoint(sketch, "E239.visualSharp", {"position": v(-13.63, 49.22) * mm});
            skArc(sketch, "E239.filletArc", {"start": v(-13.63, 48.72) * mm, "mid": v(-13.78, 49.07) * mm, "end": v(-14.13, 49.22) * mm});
            skPoint(sketch, "E240.visualSharp", {"position": v(-13.63, 46.02) * mm});
            skArc(sketch, "E240.filletArc", {"start": v(-14.13, 46.02) * mm, "mid": v(-13.78, 46.17) * mm, "end": v(-13.63, 46.52) * mm});
            skPoint(sketch, "E241.visualSharp", {"position": v(-15.63, 46.02) * mm});
            skArc(sketch, "E241.filletArc", {"start": v(-15.63, 46.52) * mm, "mid": v(-15.49, 46.17) * mm, "end": v(-15.13, 46.02) * mm});
            skPoint(sketch, "E242.visualSharp", {"position": v(-15.63, 42.02) * mm});
            skArc(sketch, "E242.filletArc", {"start": v(-15.13, 42.02) * mm, "mid": v(-15.49, 41.87) * mm, "end": v(-15.63, 41.52) * mm});
            skPoint(sketch, "E243.visualSharp", {"position": v(-13.63, 42.02) * mm});
            skArc(sketch, "E243.filletArc", {"start": v(-13.63, 41.52) * mm, "mid": v(-13.78, 41.87) * mm, "end": v(-14.13, 42.02) * mm});
            skPoint(sketch, "E244.visualSharp", {"position": v(-13.63, 38.82) * mm});
            skArc(sketch, "E244.filletArc", {"start": v(-14.13, 38.82) * mm, "mid": v(-13.78, 38.97) * mm, "end": v(-13.63, 39.32) * mm});
            skPoint(sketch, "E245.visualSharp", {"position": v(-15.63, 38.82) * mm});
            skArc(sketch, "E245.filletArc", {"start": v(-15.63, 39.32) * mm, "mid": v(-15.49, 38.97) * mm, "end": v(-15.13, 38.82) * mm});
            skPoint(sketch, "E246.visualSharp", {"position": v(-15.63, 33.82) * mm});
            skArc(sketch, "E246.filletArc", {"start": v(-15.13, 33.82) * mm, "mid": v(-15.49, 33.67) * mm, "end": v(-15.63, 33.32) * mm});
            skPoint(sketch, "E247.visualSharp", {"position": v(-13.63, 33.82) * mm});
            skArc(sketch, "E247.filletArc", {"start": v(-13.63, 33.32) * mm, "mid": v(-13.78, 33.67) * mm, "end": v(-14.13, 33.82) * mm});
            skPoint(sketch, "E248.visualSharp", {"position": v(-13.63, 30.62) * mm});
            skArc(sketch, "E248.filletArc", {"start": v(-14.13, 30.62) * mm, "mid": v(-13.78, 30.77) * mm, "end": v(-13.63, 31.12) * mm});
            skPoint(sketch, "E249.visualSharp", {"position": v(-15.63, 30.62) * mm});
            skArc(sketch, "E249.filletArc", {"start": v(-15.63, 31.12) * mm, "mid": v(-15.49, 30.77) * mm, "end": v(-15.13, 30.62) * mm});
            skArc(sketch, "E250.MirrorCS", {"start": v(14.17, 49.22) * mm, "mid": v(14.52, 49.07) * mm, "end": v(14.67, 48.72) * mm});
            skArc(sketch, "E251.MirrorCS", {"start": v(12.67, 48.72) * mm, "mid": v(12.81, 49.07) * mm, "end": v(13.17, 49.22) * mm});
            skArc(sketch, "E252.MirrorCS", {"start": v(13.17, 46.02) * mm, "mid": v(12.81, 46.17) * mm, "end": v(12.67, 46.52) * mm});
            skArc(sketch, "E253.MirrorCS", {"start": v(12.67, 33.32) * mm, "mid": v(12.81, 33.67) * mm, "end": v(13.17, 33.82) * mm});
            skArc(sketch, "E254.MirrorCS", {"start": v(14.17, 33.82) * mm, "mid": v(14.52, 33.67) * mm, "end": v(14.67, 33.32) * mm});
            skArc(sketch, "E255.MirrorCS", {"start": v(14.67, 46.52) * mm, "mid": v(14.52, 46.17) * mm, "end": v(14.17, 46.02) * mm});
            skArc(sketch, "E256.MirrorCS", {"start": v(14.67, 39.32) * mm, "mid": v(14.52, 38.97) * mm, "end": v(14.17, 38.82) * mm});
            skArc(sketch, "E257.MirrorCS", {"start": v(12.67, 41.52) * mm, "mid": v(12.81, 41.87) * mm, "end": v(13.17, 42.02) * mm});
            skArc(sketch, "E258.MirrorCS", {"start": v(14.67, 31.12) * mm, "mid": v(14.52, 30.77) * mm, "end": v(14.17, 30.62) * mm});
            skArc(sketch, "E259.MirrorCS", {"start": v(13.17, 38.82) * mm, "mid": v(12.81, 38.97) * mm, "end": v(12.67, 39.32) * mm});
            skArc(sketch, "E260.MirrorCS", {"start": v(14.17, 42.02) * mm, "mid": v(14.52, 41.87) * mm, "end": v(14.67, 41.52) * mm});
            skArc(sketch, "E261.MirrorCS", {"start": v(13.17, 30.62) * mm, "mid": v(12.81, 30.77) * mm, "end": v(12.67, 31.12) * mm});
            skPoint(sketch, "E262.MirrorP", {"position": v(14.67, 30.62) * mm});
            skPoint(sketch, "E263.MirrorP", {"position": v(14.67, 46.02) * mm});
            skPoint(sketch, "E264.MirrorP", {"position": v(12.67, 46.02) * mm});
            skPoint(sketch, "E265.MirrorP", {"position": v(12.67, 30.62) * mm});
            skLineSegment(sketch, "E266.MirrorCS", {"start": v(12.67, 33.32) * mm, "end": v(12.67, 31.12) * mm});
            skLineSegment(sketch, "E267.MirrorCS", {"start": v(14.17, 38.82) * mm, "end": v(13.17, 38.82) * mm});
            skPoint(sketch, "E268.MirrorP", {"position": v(14.67, 38.82) * mm});
            skLineSegment(sketch, "E269.MirrorCS", {"start": v(14.17, 42.02) * mm, "end": v(13.17, 42.02) * mm});
            skPoint(sketch, "E270.MirrorP", {"position": v(14.67, 42.02) * mm});
            skLineSegment(sketch, "E271.MirrorCS", {"start": v(14.67, 41.52) * mm, "end": v(14.67, 39.32) * mm});
            skLineSegment(sketch, "E272.MirrorCS", {"start": v(12.67, 48.72) * mm, "end": v(12.67, 46.52) * mm});
            skLineSegment(sketch, "E273.MirrorCS", {"start": v(14.17, 33.82) * mm, "end": v(13.17, 33.82) * mm});
            skLineSegment(sketch, "E274.MirrorCS", {"start": v(12.67, 41.52) * mm, "end": v(12.67, 39.32) * mm});
            skLineSegment(sketch, "E275.MirrorCS", {"start": v(14.17, 46.02) * mm, "end": v(13.17, 46.02) * mm});
            skPoint(sketch, "E276.MirrorP", {"position": v(14.67, 33.82) * mm});
            skPoint(sketch, "E277.MirrorP", {"position": v(14.67, 49.22) * mm});
            skPoint(sketch, "E278.MirrorP", {"position": v(12.67, 42.02) * mm});
            skLineSegment(sketch, "E279.MirrorCS", {"start": v(14.17, 49.22) * mm, "end": v(13.17, 49.22) * mm});
            skLineSegment(sketch, "E280.MirrorCS", {"start": v(14.67, 33.32) * mm, "end": v(14.67, 31.12) * mm});
            skLineSegment(sketch, "E281.MirrorCS", {"start": v(14.67, 48.72) * mm, "end": v(14.67, 46.52) * mm});
            skPoint(sketch, "E282.MirrorP", {"position": v(12.67, 49.22) * mm});
            skLineSegment(sketch, "E283.MirrorCS", {"start": v(14.17, 30.62) * mm, "end": v(13.17, 30.62) * mm});
            skPoint(sketch, "E284.MirrorP", {"position": v(12.67, 33.82) * mm});
            skPoint(sketch, "E285.MirrorP", {"position": v(12.67, 38.82) * mm});
            skLineSegment(sketch, "E286.bottom", {"start": v(-0.98, 42.05) * mm, "end": v(0.02, 42.05) * mm});
            skLineSegment(sketch, "E286.top", {"start": v(-0.98, 38.85) * mm, "end": v(0.02, 38.85) * mm});
            skLineSegment(sketch, "E286.left", {"start": v(-1.48, 41.55) * mm, "end": v(-1.48, 39.35) * mm});
            skLineSegment(sketch, "E286.right", {"start": v(0.52, 41.55) * mm, "end": v(0.52, 39.35) * mm});
            skPoint(sketch, "E287.visualSharp", {"position": v(-1.48, 42.05) * mm});
            skArc(sketch, "E287.filletArc", {"start": v(-0.98, 42.05) * mm, "mid": v(-1.34, 41.9) * mm, "end": v(-1.48, 41.55) * mm});
            skPoint(sketch, "E288.visualSharp", {"position": v(0.52, 42.05) * mm});
            skArc(sketch, "E288.filletArc", {"start": v(0.52, 41.55) * mm, "mid": v(0.37, 41.9) * mm, "end": v(0.02, 42.05) * mm});
            skPoint(sketch, "E289.visualSharp", {"position": v(0.52, 38.85) * mm});
            skArc(sketch, "E289.filletArc", {"start": v(0.02, 38.85) * mm, "mid": v(0.37, 39) * mm, "end": v(0.52, 39.35) * mm});
            skPoint(sketch, "E290.visualSharp", {"position": v(-1.48, 38.85) * mm});
            skArc(sketch, "E290.filletArc", {"start": v(-1.48, 39.35) * mm, "mid": v(-1.34, 39) * mm, "end": v(-0.98, 38.85) * mm});
            skLineSegment(sketch, "E291.bottom", {"start": v(-0.98, 35.85) * mm, "end": v(0.02, 35.85) * mm});
            skLineSegment(sketch, "E291.top", {"start": v(-0.98, 32.65) * mm, "end": v(0.02, 32.65) * mm});
            skLineSegment(sketch, "E291.left", {"start": v(-1.48, 35.35) * mm, "end": v(-1.48, 33.15) * mm});
            skLineSegment(sketch, "E291.right", {"start": v(0.52, 35.35) * mm, "end": v(0.52, 33.15) * mm});
            skPoint(sketch, "E292.visualSharp", {"position": v(-1.48, 35.85) * mm});
            skArc(sketch, "E292.filletArc", {"start": v(-0.98, 35.85) * mm, "mid": v(-1.34, 35.7) * mm, "end": v(-1.48, 35.35) * mm});
            skPoint(sketch, "E293.visualSharp", {"position": v(0.52, 35.85) * mm});
            skArc(sketch, "E293.filletArc", {"start": v(0.52, 35.35) * mm, "mid": v(0.37, 35.7) * mm, "end": v(0.02, 35.85) * mm});
            skPoint(sketch, "E294.visualSharp", {"position": v(0.52, 32.65) * mm});
            skArc(sketch, "E294.filletArc", {"start": v(0.02, 32.65) * mm, "mid": v(0.37, 32.8) * mm, "end": v(0.52, 33.15) * mm});
            skPoint(sketch, "E295.visualSharp", {"position": v(-1.48, 32.65) * mm});
            skArc(sketch, "E295.filletArc", {"start": v(-1.48, 33.15) * mm, "mid": v(-1.34, 32.8) * mm, "end": v(-0.98, 32.65) * mm});
            skLineSegment(sketch, "E296.bottom", {"start": v(-0.98, 29.15) * mm, "end": v(0.02, 29.15) * mm});
            skLineSegment(sketch, "E296.top", {"start": v(-0.98, 25.95) * mm, "end": v(0.02, 25.95) * mm});
            skLineSegment(sketch, "E296.left", {"start": v(-1.48, 28.65) * mm, "end": v(-1.48, 26.45) * mm});
            skLineSegment(sketch, "E296.right", {"start": v(0.52, 28.65) * mm, "end": v(0.52, 26.45) * mm});
            skPoint(sketch, "E297.visualSharp", {"position": v(-1.48, 29.15) * mm});
            skArc(sketch, "E297.filletArc", {"start": v(-0.98, 29.15) * mm, "mid": v(-1.34, 29) * mm, "end": v(-1.48, 28.65) * mm});
            skPoint(sketch, "E298.visualSharp", {"position": v(0.52, 29.15) * mm});
            skArc(sketch, "E298.filletArc", {"start": v(0.52, 28.65) * mm, "mid": v(0.37, 29) * mm, "end": v(0.02, 29.15) * mm});
            skPoint(sketch, "E299.visualSharp", {"position": v(0.52, 25.95) * mm});
            skArc(sketch, "E299.filletArc", {"start": v(0.02, 25.95) * mm, "mid": v(0.37, 26.1) * mm, "end": v(0.52, 26.45) * mm});
            skPoint(sketch, "E300.visualSharp", {"position": v(-1.48, 25.95) * mm});
            skArc(sketch, "E300.filletArc", {"start": v(-1.48, 26.45) * mm, "mid": v(-1.34, 26.1) * mm, "end": v(-0.98, 25.95) * mm});
            skSolve(sketch);
        }
        {
            var Q0;
            Q0 = qSketchRegion(id + "F0", true);
            extrude(context, id + "F1", {"entities" : qUnion([Q0]), "depth" : 1.5 * mm, "offsetDistance" : 25.4 * mm});
        }
    });
